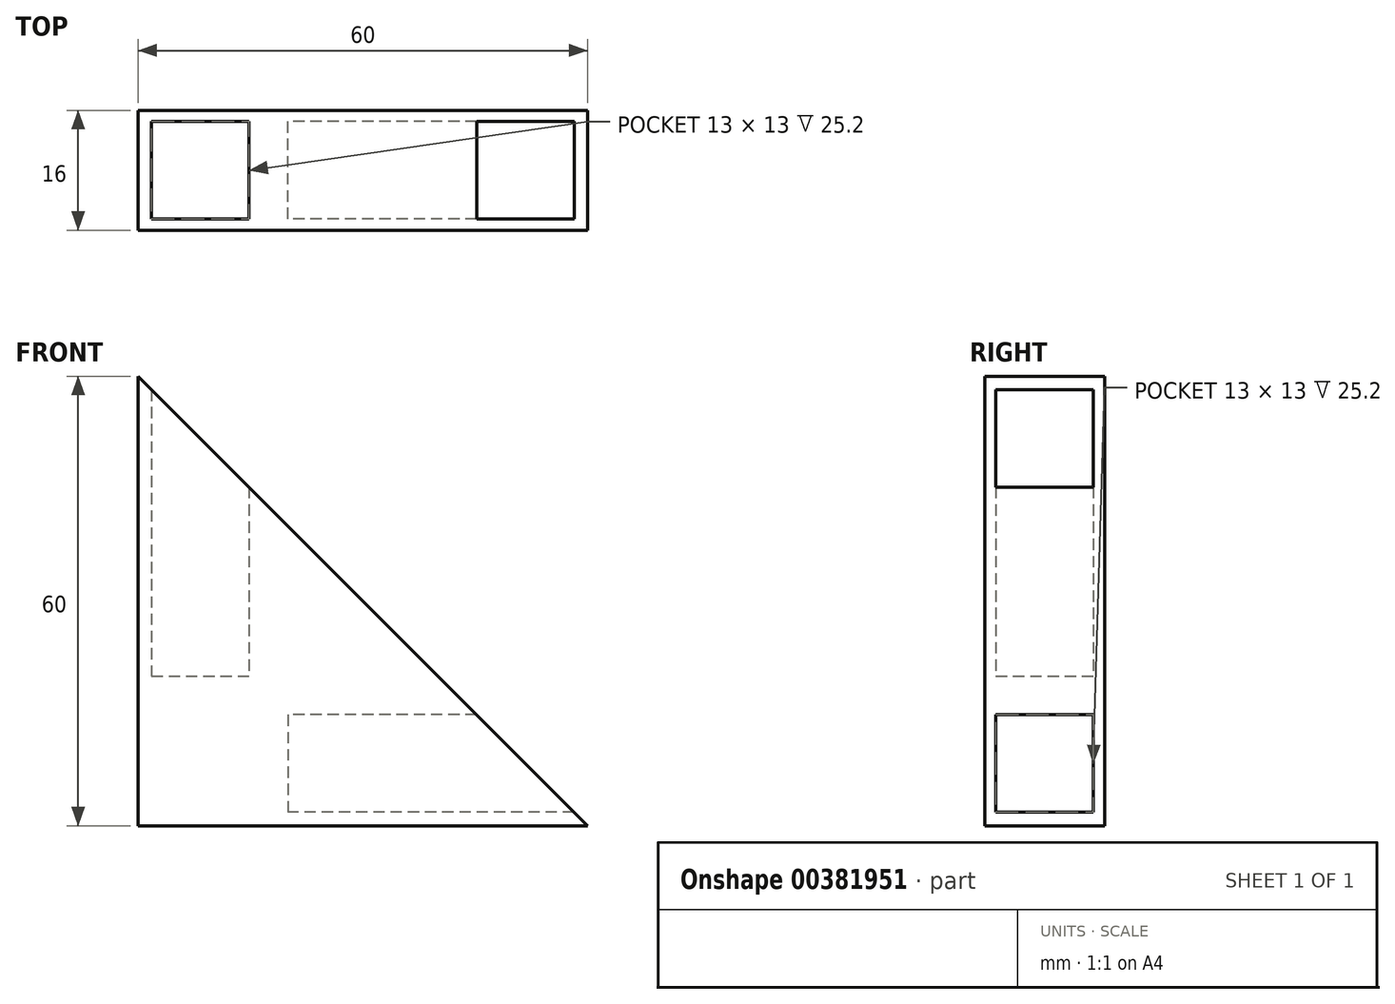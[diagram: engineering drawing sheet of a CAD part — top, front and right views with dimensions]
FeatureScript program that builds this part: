
annotation { "Feature Type Name" : "Feature", "Feature Type Description" : "" }
export const myFeature = defineFeature(function(context is Context, id is Id, definition is map)
    precondition{}
    {
        {
            var Q0;
            Q0=qCreatedBy(makeId("Front.planeOp"),FACE);
            var sketch = newSketch(context, id + "F0", { "sketchPlane" : qUnion([Q0])});
            skLineSegment(sketch, "E0", {"start": v(0, 0) * mm, "end": v(0, 60) * mm});
            skLineSegment(sketch, "E1", {"start": v(0, 60) * mm, "end": v(60, 0) * mm});
            skLineSegment(sketch, "E2", {"start": v(60, 0) * mm, "end": v(0, 0) * mm});
            skSolve(sketch);
        }
        {
            var Q0;
            Q0 = qSketchRegion(id + "F0", true);
            extrude(context, id + "F1", {"entities" : qUnion([Q0]), "depth" : 16 * mm});
        }
        {
            var Q0;
            Q0=makeQuery(id+"F1.opExtrude","CAP_FACE",FACE,{"disambiguationData":[OSD([sQuery(id+"F0.wireOp",EDGE,"E0"),sQuery(id+"F0.wireOp",EDGE,"E1"),sQuery(id+"F0.wireOp",EDGE,"E2")])],"isStart":true});
            var sketch = newSketch(context, id + "F2", { "sketchPlane" : qUnion([Q0])});
            skLineSegment(sketch, "E3.bottom", {"start": v(-1.8, 69.4) * mm, "end": v(-14.8, 69.4) * mm});
            skLineSegment(sketch, "E3.top", {"start": v(-1.8, 20) * mm, "end": v(-14.8, 20) * mm});
            skLineSegment(sketch, "E3.left", {"start": v(-1.8, 69.4) * mm, "end": v(-1.8, 20) * mm});
            skLineSegment(sketch, "E3.right", {"start": v(-14.8, 69.4) * mm, "end": v(-14.8, 20) * mm});
            skLineSegment(sketch, "E4.bottom", {"start": v(-73.92, 14.8) * mm, "end": v(-20, 14.8) * mm});
            skLineSegment(sketch, "E4.top", {"start": v(-73.92, 1.8) * mm, "end": v(-20, 1.8) * mm});
            skLineSegment(sketch, "E4.left", {"start": v(-73.92, 14.8) * mm, "end": v(-73.92, 1.8) * mm});
            skLineSegment(sketch, "E4.right", {"start": v(-20, 14.8) * mm, "end": v(-20, 1.8) * mm});
            skSolve(sketch);
        }
        {
            var Q0;
            Q0 = qSketchRegion(id + "F2", true);
            extrude(context, id + "F3", {"entities" : qUnion([Q0]), "operationType" : NewBodyOperationType.REMOVE, "oppositeDirection" : true, "depth" : 14.5 * mm, "hasSecondDirection" : true, "secondDirectionOppositeDirection" : true, "secondDirectionDepth" : 1.5 * mm});
        }
    });
